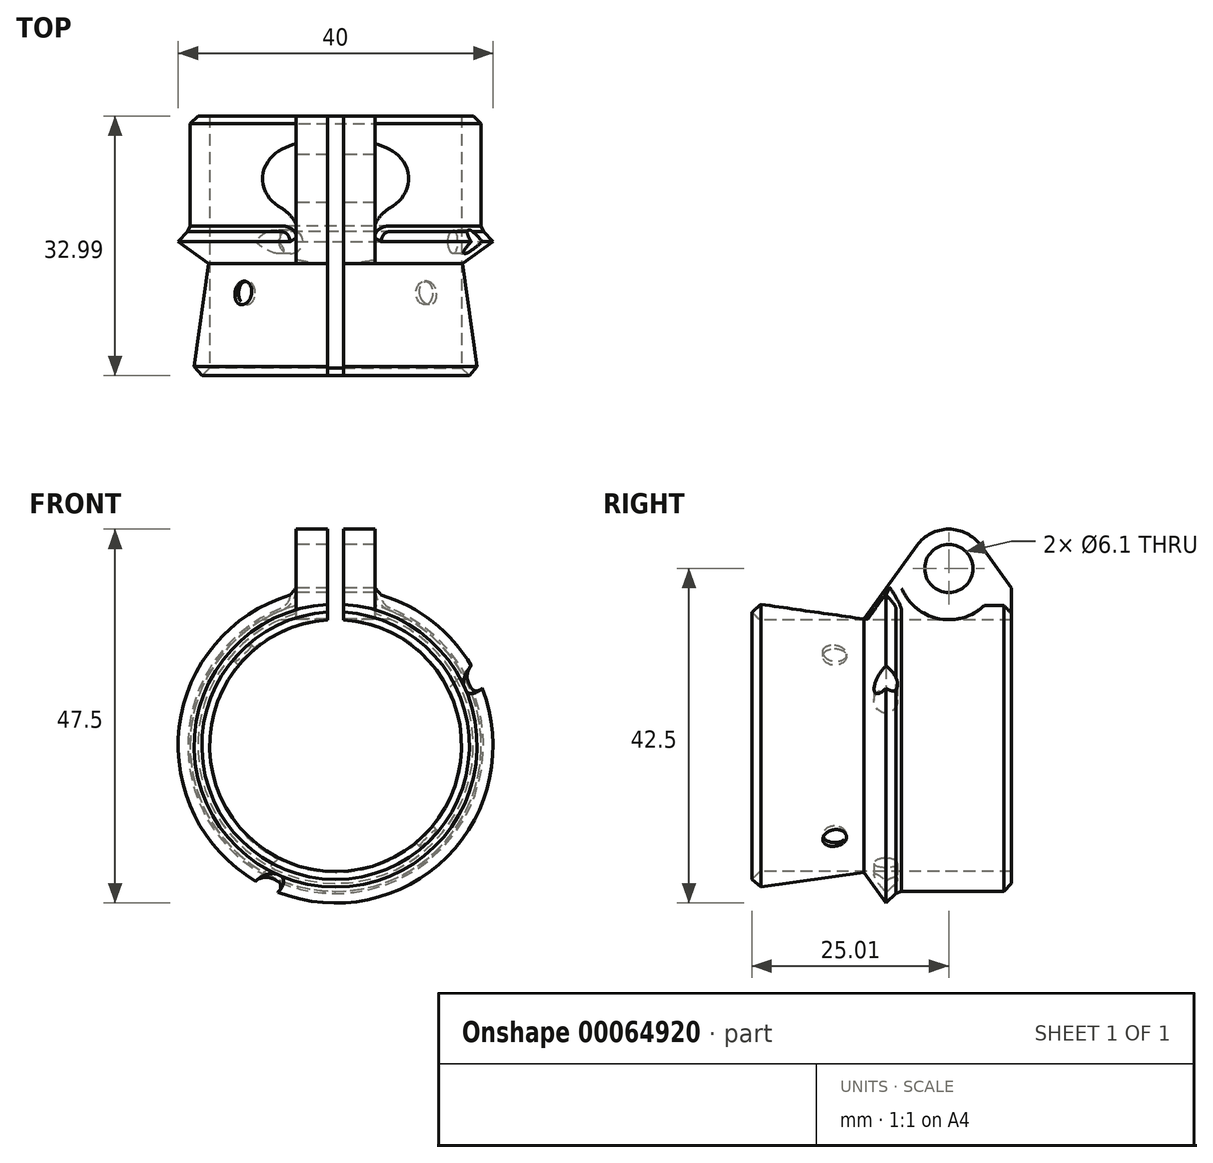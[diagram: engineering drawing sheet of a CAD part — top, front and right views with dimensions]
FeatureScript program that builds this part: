
annotation { "Feature Type Name" : "Feature", "Feature Type Description" : "" }
export const myFeature = defineFeature(function(context is Context, id is Id, definition is map)
    precondition{}
    {
        {
            var Q0;
            Q0=qCreatedBy(makeId("Right.planeOp"),FACE);
            var sketch = newSketch(context, id + "F0", { "sketchPlane" : qUnion([Q0])});
            skLineSegment(sketch, "E0", {"start": v(-73.5, 0) * mm, "end": v(75.24, 0) * mm});
            skLineSegment(sketch, "E1.0", {"start": v(15.98, 0) * mm, "end": v(15.98, 57.64) * mm});
            skLineSegment(sketch, "E2.0", {"start": v(-17.02, 0) * mm, "end": v(-17.02, 57.64) * mm});
            skLineSegment(sketch, "E3.0", {"start": v(-73.5, 15) * mm, "end": v(-17.02, 15) * mm});
            skLineSegment(sketch, "E4.0", {"start": v(-73.5, 20) * mm, "end": v(-17.02, 20) * mm});
            skLineSegment(sketch, "E5.trimOffspring", {"start": v(15.98, 20) * mm, "end": v(75.24, 20) * mm});
            skCircle(sketch, "E6", {"center": v(8, 22.5) * mm, "radius": 3.05 * mm});
            skArc(sketch, "E7", {"start": v(12.05, 25.43) * mm, "mid": v(8, 27.5) * mm, "end": v(3.95, 25.43) * mm});
            skLineSegment(sketch, "E8", {"start": v(0.02, 20) * mm, "end": v(3.95, 25.43) * mm});
            skLineSegment(sketch, "E9", {"start": v(15.98, 20) * mm, "end": v(12.05, 25.43) * mm});
            skPoint(sketch, "E10.orphan", {"position": v(8, 17.5) * mm});
            skLineSegment(sketch, "E11", {"start": v(0.8, 21.1) * mm, "end": v(-2.8, 16.12) * mm});
            skLineSegment(sketch, "E12", {"start": v(-2.8, 16.12) * mm, "end": v(15.98, 16.12) * mm});
            skLineSegment(sketch, "E13", {"start": v(15.98, 20) * mm, "end": v(15.98, 16.12) * mm});
            skLineSegment(sketch, "E14", {"start": v(-17.02, 20) * mm, "end": v(0.02, 20) * mm});
            skLineSegment(sketch, "E15", {"start": v(0.02, 20) * mm, "end": v(1.6, 18.5) * mm});
            skLineSegment(sketch, "E16.0", {"start": v(-73.5, 16) * mm, "end": v(75.24, 16) * mm});
            skLineSegment(sketch, "E17.trimOffspring", {"start": v(15.98, 15) * mm, "end": v(75.24, 15) * mm});
            skLineSegment(sketch, "E18.0", {"start": v(15.98, 18.5) * mm, "end": v(1.6, 18.5) * mm});
            skLineSegment(sketch, "E19", {"start": v(-17.02, 20) * mm, "end": v(6.52, 27.28) * mm});
            skLineSegment(sketch, "E20", {"start": v(-17.02, 20) * mm, "end": v(-17.02, 18.13) * mm});
            skLineSegment(sketch, "E21", {"start": v(-17.02, 18.13) * mm, "end": v(-2.8, 16.12) * mm});
            skSolve(sketch);
        }
        {
            var Q0;
            {var subQ0=sQuery(id+"F0.wireOp",EDGE,"umc4HKQ1-BMdF-l6FB-0X5F-qHgtKlofnmGQ");Q0=makeQuery(id+"F0.imprint","IMPRINT",FACE,{"disambiguationData":[TD([[makeQuery(id+"F0.imprint","IMPRINT",EDGE,{"derivedFrom":subQ0}),1.0]])]});}
            var Q1;
            {var subQ0=sQuery(id+"F0.wireOp",EDGE,"sHcc5p6c-mAEp-OemM-725t-415vjHjdboY6");Q1=makeQuery(id+"F0.imprint","IMPRINT",FACE,{"disambiguationData":[TD([[makeQuery(id+"F0.imprint","IMPRINT",EDGE,{"derivedFrom":subQ0}),-1.0]])]});}
            var Q2;
            {var subQ2=sQuery(id+"F0.wireOp",EDGE,"E12");Q2=makeQuery(id+"F0.imprint","IMPRINT",FACE,{"disambiguationData":[TD([[makeQuery(id+"F0.imprint","IMPRINT",EDGE,{"derivedFrom":subQ2}),-1.0]])]});}
            var Q3;
            {var subQ1=sQuery(id+"F0.wireOp",EDGE,"E12");Q3=makeQuery(id+"F0.imprint","IMPRINT",FACE,{"disambiguationData":[TD([[makeQuery(id+"F0.imprint","IMPRINT",EDGE,{"derivedFrom":subQ1}),1.0]])]});}
            var Q4;
            Q4=sQuery(id+"F0.wireOp",EDGE,"E0");
            revolve(context, id + "F1", {"entities" : qUnion([Q0, Q1, Q2, Q3]), "axis" : qUnion([Q4]), "revolveType" : RevolveType.FULL});
        }
        {
            var Q0;
            Q0=qCreatedBy(makeId("Top.planeOp"),FACE);
            var sketch = newSketch(context, id + "F2", { "sketchPlane" : qUnion([Q0])});
            skLineSegment(sketch, "E22.0", {"start": v(-1, 21.77) * mm, "end": v(-1, -19.87) * mm});
            skLineSegment(sketch, "E23.0", {"start": v(1, 21.77) * mm, "end": v(1, -19.87) * mm});
            skLineSegment(sketch, "E24", {"start": v(-1, 21.77) * mm, "end": v(1, 21.77) * mm});
            skLineSegment(sketch, "E25", {"start": v(-1, -19.87) * mm, "end": v(1, -19.87) * mm});
            skPoint(sketch, "E26.orphan", {"position": v(0, 31.98) * mm});
            skSolve(sketch);
        }
        {
            var Q0;
            Q0=makeQuery(id+"F0.imprint","IMPRINT",FACE,{"disambiguationData":[TD([[makeQuery(id+"F0.imprint","IMPRINT",EDGE,{"derivedFrom":sQuery(id+"F0.wireOp",EDGE,"E6")}),-1.0]])]});
            var Q1;
            {var subQ1=sQuery(id+"F0.wireOp",EDGE,"E12");Q1=makeQuery(id+"F0.imprint","IMPRINT",FACE,{"disambiguationData":[TD([[makeQuery(id+"F0.imprint","IMPRINT",EDGE,{"derivedFrom":subQ1}),1.0]])]});}
            extrude(context, id + "F3", {"entities" : qUnion([Q0, Q1]), "operationType" : NewBodyOperationType.ADD, "depth" : 10 * mm, "symmetric" : true});
        }
        {
            var Q0;
            Q0 = qSketchRegion(id + "F2", true);
            extrude(context, id + "F4", {"entities" : qUnion([Q0]), "operationType" : NewBodyOperationType.REMOVE, "depth" : 30 * mm});
        }
        {
            var Q0;
            Q0=qCreatedBy(makeId("Front.planeOp"),FACE);
            cPlane(context, id + "F5", {"entities" : qUnion([Q0]), "cplaneType" : CPlaneType.OFFSET, "offset" : 5 * mm, "width" : 150 * mm, "height" : 150 * mm});
        }
        {
            var Q0;
            Q0=qCreatedBy(id+"F5.planeOp",FACE);
            var sketch = newSketch(context, id + "F6", { "sketchPlane" : qUnion([Q0])});
            skLineSegment(sketch, "E27", {"start": v(0, 0) * mm, "end": v(0, -29.29) * mm});
            skLineSegment(sketch, "E28", {"start": v(0, 0) * mm, "end": v(-37.54, 0) * mm});
            skLineSegment(sketch, "E29", {"start": v(-14.14, -14.14) * mm, "end": v(14.14, 14.14) * mm});
            skArc(sketch, "E30.0", {"start": v(1, 19.97) * mm, "mid": v(0, -20) * mm, "end": v(-1, 19.97) * mm});
            skLineSegment(sketch, "E31", {"start": v(0, 0) * mm, "end": v(14.14, -14.14) * mm});
            skLineSegment(sketch, "E32", {"start": v(14.14, -14.14) * mm, "end": v(-14.14, 14.14) * mm});
            skSolve(sketch);
        }
        {
            var Q0;
            Q0=sQuery(id+"F6.wireOp",EDGE,"E29");
            cPlane(context, id + "F7", {"entities" : qUnion([Q0]), "cplaneType" : CPlaneType.MID_PLANE, "offset" : 150 * mm, "width" : 150 * mm, "height" : 150 * mm});
        }
        {
            var Q0;
            Q0=qCreatedBy(id+"F7.planeOp",FACE);
            var sketch = newSketch(context, id + "F8", { "sketchPlane" : qUnion([Q0])});
            skLineSegment(sketch, "E33", {"start": v(0, 0) * mm, "end": v(0, -12.96) * mm});
            skLineSegment(sketch, "E34", {"start": v(0, -6.5) * mm, "end": v(-5.98, -6.5) * mm});
            skCircle(sketch, "E35", {"center": v(0, -6.5) * mm, "radius": 1.5 * mm});
            skSolve(sketch);
        }
        {
            var Q0;
            Q0 = qSketchRegion(id + "F8", true);
            extrude(context, id + "F9", {"entities" : qUnion([Q0]), "operationType" : NewBodyOperationType.REMOVE, "depth" : 50 * mm, "symmetric" : true});
        }
        {
            var Q0;
            Q0=sQuery(id+"F6.wireOp",EDGE,"E32");
            cPlane(context, id + "F10", {"entities" : qUnion([Q0]), "cplaneType" : CPlaneType.MID_PLANE, "offset" : 150 * mm, "width" : 150 * mm, "height" : 150 * mm});
        }
        {
            var Q0;
            Q0=qCreatedBy(id+"F10.planeOp",FACE);
            var sketch = newSketch(context, id + "F11", { "sketchPlane" : qUnion([Q0])});
            skLineSegment(sketch, "E36", {"start": v(0, 0) * mm, "end": v(6.5, 0) * mm});
            skCircle(sketch, "E37", {"center": v(6.5, 0) * mm, "radius": 1.5 * mm});
            skSolve(sketch);
        }
        {
            var Q0;
            Q0 = qSketchRegion(id + "F11", true);
            extrude(context, id + "F12", {"entities" : qUnion([Q0]), "operationType" : NewBodyOperationType.REMOVE, "oppositeDirection" : true, "depth" : 50 * mm, "symmetric" : true});
        }
        {
            var Q0;
            Q0=makeQuery(id+"F3.opExtrude","CAP_FACE",FACE,{"disambiguationData":[OSD([sQuery(id+"F0.wireOp",EDGE,"E6"),sQuery(id+"F0.wireOp",EDGE,"E7"),sQuery(id+"F0.wireOp",EDGE,"E8"),sQuery(id+"F0.wireOp",EDGE,"E9"),sQuery(id+"F0.wireOp",EDGE,"E11"),sQuery(id+"F0.wireOp",EDGE,"E12"),sQuery(id+"F0.wireOp",EDGE,"E13")])],"isStart":false});
            var sketch = newSketch(context, id + "F13", { "sketchPlane" : qUnion([Q0])});
            skCircle(sketch, "E38", {"center": v(8, 22.5) * mm, "radius": 6.5 * mm});
            skSolve(sketch);
        }
        {
            var Q0;
            Q0 = qSketchRegion(id + "F13", true);
            extrude(context, id + "F14", {"entities" : qUnion([Q0]), "operationType" : NewBodyOperationType.REMOVE, "depth" : 25 * mm});
        }
        {
            var Q0;
            Q0=makeQuery(id+"F3.opExtrude","CAP_FACE",FACE,{"disambiguationData":[OSD([sQuery(id+"F0.wireOp",EDGE,"E6"),sQuery(id+"F0.wireOp",EDGE,"E7"),sQuery(id+"F0.wireOp",EDGE,"E8"),sQuery(id+"F0.wireOp",EDGE,"E9"),sQuery(id+"F0.wireOp",EDGE,"E11"),sQuery(id+"F0.wireOp",EDGE,"E12"),sQuery(id+"F0.wireOp",EDGE,"E13")])],"isStart":true});
            var sketch = newSketch(context, id + "F15", { "sketchPlane" : qUnion([Q0])});
            skCircle(sketch, "E39", {"center": v(-8, 22.5) * mm, "radius": 6.5 * mm});
            skSolve(sketch);
        }
        {
            var Q0;
            Q0 = qSketchRegion(id + "F15", true);
            extrude(context, id + "F16", {"entities" : qUnion([Q0]), "operationType" : NewBodyOperationType.REMOVE, "depth" : 25 * mm});
        }
        {
            var Q0;
            {var subQ1=makeQuery(id+"F3.opExtrude","CAP_FACE",FACE,{"disambiguationData":[OSD([sQuery(id+"F0.wireOp",EDGE,"E6"),sQuery(id+"F0.wireOp",EDGE,"E7"),sQuery(id+"F0.wireOp",EDGE,"E8"),sQuery(id+"F0.wireOp",EDGE,"E9"),sQuery(id+"F0.wireOp",EDGE,"E11"),sQuery(id+"F0.wireOp",EDGE,"E12"),sQuery(id+"F0.wireOp",EDGE,"E13")])],"isStart":false});var subQ2=makeQuery(id+"F1.opRevolve","SWEPT_FACE",FACE,{"disambiguationData":[OSD([sQuery(id+"F0.wireOp",EDGE,"E18.0")])]});Q0=makeQuery(id+"F14.boolean.opBoolean","SPLIT",EDGE,{"disambiguationData":[TD([makeQuery(id+"F1.opRevolve","SWEPT_FACE",FACE,{"disambiguationData":[OSD([sQuery(id+"F0.wireOp",EDGE,"E15")])]})])],"derivedFrom":makeQuery(id+"F3.boolean.opBoolean","INTERSECT",EDGE,{"derivedFrom":[subQ2,subQ1]})});}
            var Q1;
            {var subQ0=sQuery(id+"F0.wireOp",EDGE,"E18.0");var subQ1=sQuery(id+"F0.wireOp",EDGE,"E13");var subQ2=makeQuery(id+"F1.opRevolve","SWEPT_FACE",FACE,{"disambiguationData":[OSD([subQ0])]});var subQ3=makeQuery(id+"F3.opExtrude","CAP_FACE",FACE,{"disambiguationData":[OSD([sQuery(id+"F0.wireOp",EDGE,"E6"),sQuery(id+"F0.wireOp",EDGE,"E7"),sQuery(id+"F0.wireOp",EDGE,"E8"),sQuery(id+"F0.wireOp",EDGE,"E9"),sQuery(id+"F0.wireOp",EDGE,"E11"),sQuery(id+"F0.wireOp",EDGE,"E12"),subQ1])],"isStart":false});Q1=makeQuery(id+"F14.boolean.opBoolean","SPLIT",EDGE,{"disambiguationData":[TD([makeQuery(id+"FXoMnwHVasLWueJ_1.opChamfer","BLEND_FACE",FACE,{"disambiguationData":[OSD([subQ1]),TDD([makeQuery(id+"F3.opExtrude","CAP_EDGE",EDGE,{"disambiguationData":[OSD([subQ1])],"isStart":false})])]})])],"derivedFrom":makeQuery(id+"F3.boolean.opBoolean","INTERSECT",EDGE,{"derivedFrom":[subQ2,subQ3]})});}
            var Q2;
            {var subQ1=makeQuery(id+"F3.opExtrude","CAP_FACE",FACE,{"disambiguationData":[OSD([sQuery(id+"F0.wireOp",EDGE,"E6"),sQuery(id+"F0.wireOp",EDGE,"E7"),sQuery(id+"F0.wireOp",EDGE,"E8"),sQuery(id+"F0.wireOp",EDGE,"E9"),sQuery(id+"F0.wireOp",EDGE,"E11"),sQuery(id+"F0.wireOp",EDGE,"E12"),sQuery(id+"F0.wireOp",EDGE,"E13")])],"isStart":true});var subQ2=makeQuery(id+"F1.opRevolve","SWEPT_FACE",FACE,{"disambiguationData":[OSD([sQuery(id+"F0.wireOp",EDGE,"E18.0")])]});Q2=makeQuery(id+"F16.boolean.opBoolean","SPLIT",EDGE,{"disambiguationData":[TD([makeQuery(id+"F1.opRevolve","SWEPT_FACE",FACE,{"disambiguationData":[OSD([sQuery(id+"F0.wireOp",EDGE,"E15")])]})])],"derivedFrom":makeQuery(id+"F3.boolean.opBoolean","INTERSECT",EDGE,{"derivedFrom":[subQ2,subQ1]})});}
            var Q3;
            {var subQ0=sQuery(id+"F0.wireOp",EDGE,"E18.0");var subQ1=sQuery(id+"F0.wireOp",EDGE,"E13");var subQ2=makeQuery(id+"F1.opRevolve","SWEPT_FACE",FACE,{"disambiguationData":[OSD([subQ0])]});var subQ4=makeQuery(id+"F3.opExtrude","CAP_FACE",FACE,{"disambiguationData":[OSD([sQuery(id+"F0.wireOp",EDGE,"E6"),sQuery(id+"F0.wireOp",EDGE,"E7"),sQuery(id+"F0.wireOp",EDGE,"E8"),sQuery(id+"F0.wireOp",EDGE,"E9"),sQuery(id+"F0.wireOp",EDGE,"E11"),sQuery(id+"F0.wireOp",EDGE,"E12"),subQ1])],"isStart":true});Q3=makeQuery(id+"F16.boolean.opBoolean","SPLIT",EDGE,{"disambiguationData":[TD([makeQuery(id+"FXoMnwHVasLWueJ_1.opChamfer","BLEND_FACE",FACE,{"disambiguationData":[OSD([subQ1]),TDD([makeQuery(id+"F3.opExtrude","CAP_EDGE",EDGE,{"disambiguationData":[OSD([subQ1])],"isStart":true})])]})])],"derivedFrom":makeQuery(id+"F3.boolean.opBoolean","INTERSECT",EDGE,{"derivedFrom":[subQ2,subQ4]})});}
            fillet(context, id + "F17", {"entities" : qUnion([Q0, Q1, Q2, Q3]), "radius" : 3 * mm, "allowEdgeOverflow" : false});
        }
        {
            var Q0;
            Q0=makeQuery(id+"F1.opRevolve","SWEPT_EDGE",EDGE,{"disambiguationData":[OSD([sQuery(id+"F0.wireOp",EDGE,"E2.0"),sQuery(id+"F0.wireOp",EDGE,"E14")])]});
            var Q1;
            Q1=makeQuery(id+"F1.opRevolve","SWEPT_EDGE",EDGE,{"disambiguationData":[OSD([sQuery(id+"F0.wireOp",EDGE,"E13"),sQuery(id+"F0.wireOp",EDGE,"E18.0")])]});
            chamfer(context, id + "F18", {"entities" : qUnion([Q0, Q1]), "width" : 1 * mm, "tangentPropagation" : true});
        }
    });
